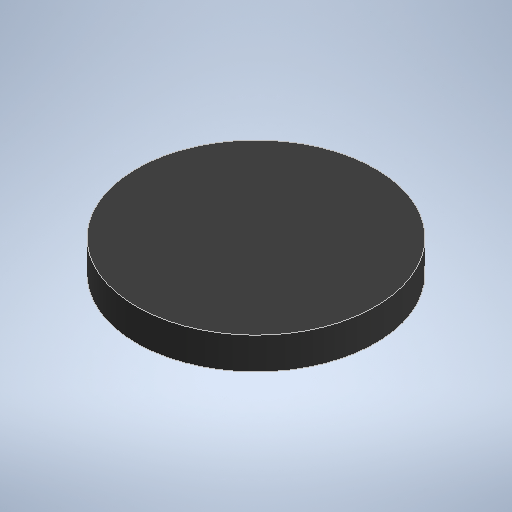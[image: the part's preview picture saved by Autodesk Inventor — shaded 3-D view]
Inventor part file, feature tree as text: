
AUTODESK INVENTOR PART (.ipt)
format: ipt  version: 2025.1 (Build 291241020, 241B)  size: 215,552 bytes
history: native  units: mm
features: other x1, extrude x1, sketch x1
ambient origin geometry x8: Origin, YZ Plane, XZ Plane, XY Plane, X Axis, Y Axis, Z Axis, Center Point
bodies: Body1 (feature_tree)
feature tree (3):
  other  "Sólido1"
  extrude  "Extrusão1"  Depth=1.0mm TaperAngle=0.0deg
  sketch  "Esboço1"  dims[d0=7.5mm d1=1.0mm d2=0.0mm]
